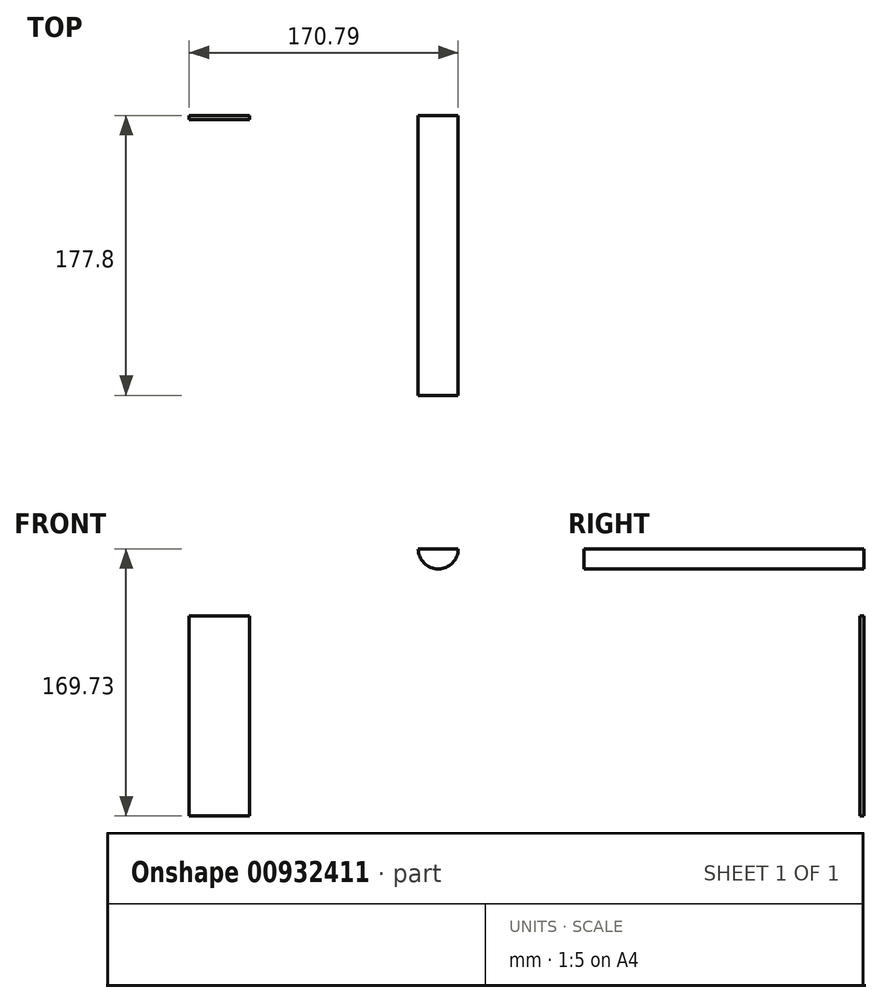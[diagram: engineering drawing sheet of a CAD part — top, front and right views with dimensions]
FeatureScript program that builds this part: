
annotation { "Feature Type Name" : "Feature", "Feature Type Description" : "" }
export const myFeature = defineFeature(function(context is Context, id is Id, definition is map)
    precondition{}
    {
        {
            var Q0;
            Q0=qCreatedBy(makeId("Front.planeOp"),FACE);
            var sketch = newSketch(context, id + "F0", { "sketchPlane" : qUnion([Q0])});
            skLineSegment(sketch, "E0.bottom", {"start": v(-55.57, -4.4) * mm, "end": v(-17.47, -4.4) * mm});
            skLineSegment(sketch, "E0.top", {"start": v(-55.57, -131.4) * mm, "end": v(-17.47, -131.4) * mm});
            skLineSegment(sketch, "E0.left", {"start": v(-55.57, -4.4) * mm, "end": v(-55.57, -131.4) * mm});
            skLineSegment(sketch, "E0.right", {"start": v(-17.47, -4.4) * mm, "end": v(-17.47, -131.4) * mm});
            skArc(sketch, "E1", {"start": v(89.82, 38.32) * mm, "mid": v(102.52, 25.62) * mm, "end": v(115.22, 38.32) * mm});
            skLineSegment(sketch, "E2", {"start": v(102.52, 38.32) * mm, "end": v(115.22, 38.32) * mm});
            skLineSegment(sketch, "E3", {"start": v(115.22, 38.32) * mm, "end": v(89.82, 38.32) * mm});
            skSolve(sketch);
        }
        {
            var Q0;
            Q0=makeQuery(id+"F0.imprint","IMPRINT",FACE,{"disambiguationData":[TD([[makeQuery(id+"F0.imprint","IMPRINT",EDGE,{"derivedFrom":sQuery(id+"F0.wireOp",EDGE,"E0.bottom")}),-1.0]])]});
            extrude(context, id + "F1", {"entities" : qUnion([Q0]), "depth" : 2.54 * mm, "offsetDistance" : 25.4 * mm});
        }
        {
            var Q0;
            Q0=makeQuery(id+"F0.imprint","IMPRINT",FACE,{"disambiguationData":[TD([[makeQuery(id+"F0.imprint","IMPRINT",EDGE,{"derivedFrom":sQuery(id+"F0.wireOp",EDGE,"E1")}),1.0]])]});
            extrude(context, id + "F2", {"entities" : qUnion([Q0]), "depth" : 177.8 * mm, "offsetDistance" : 25.4 * mm});
        }
    });
